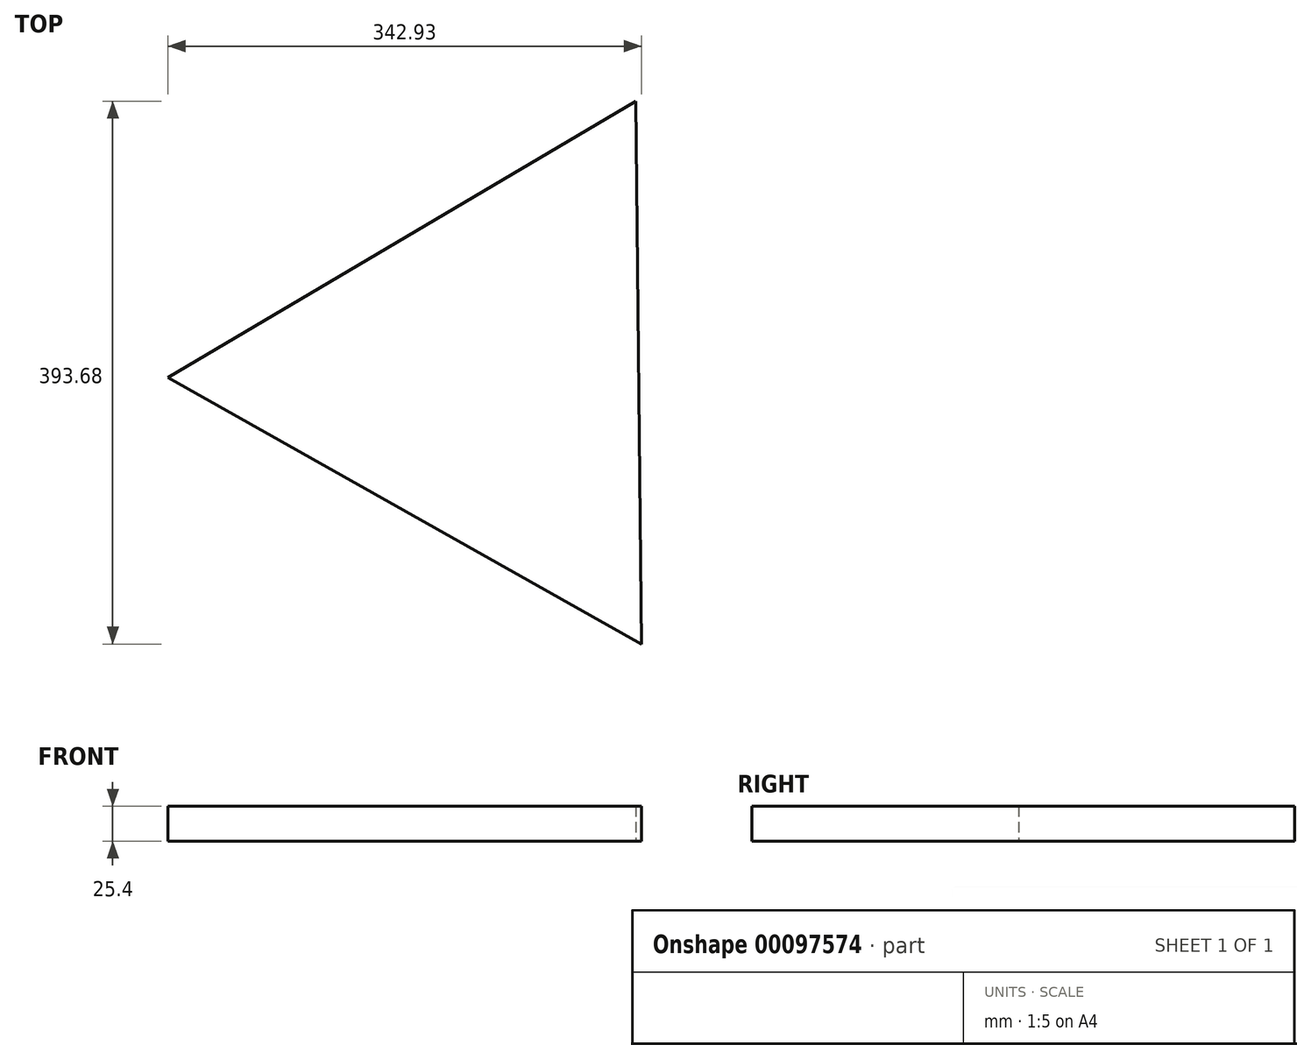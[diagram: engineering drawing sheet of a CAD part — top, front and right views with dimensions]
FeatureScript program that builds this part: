
annotation { "Feature Type Name" : "Feature", "Feature Type Description" : "" }
export const myFeature = defineFeature(function(context is Context, id is Id, definition is map)
    precondition{}
    {
        {
            var Q0;
            Q0=qCreatedBy(makeId("Top.planeOp"),FACE);
            var sketch = newSketch(context, id + "F0", { "sketchPlane" : qUnion([Q0])});
            skCircle(sketch, "E0.cCircle", {"center": v(0, 0) * mm, "radius": 113.65 * mm, "construction": true});
            skLineSegment(sketch, "E0.0", {"start": v(-227.3, -2.3) * mm, "end": v(111.66, 197.99) * mm});
            skLineSegment(sketch, "E0.1", {"start": v(111.66, 197.99) * mm, "end": v(115.64, -195.7) * mm});
            skLineSegment(sketch, "E0.2", {"start": v(115.64, -195.7) * mm, "end": v(-227.3, -2.3) * mm});
            skPoint(sketch, "E0.0.midPoint", {"position": v(-57.82, 97.85) * mm});
            skSolve(sketch);
        }
        {
            var Q0;
            Q0=makeQuery(id+"F0.imprint","IMPRINT",FACE,{"disambiguationData":[TD([[makeQuery(id+"F0.imprint","IMPRINT",EDGE,{"derivedFrom":sQuery(id+"F0.wireOp",EDGE,"E0.0")}),-1.0]])]});
            extrude(context, id + "F1", {"entities" : qUnion([Q0]), "depth" : 25.4 * mm, "offsetDistance" : 25.4 * mm});
        }
    });
